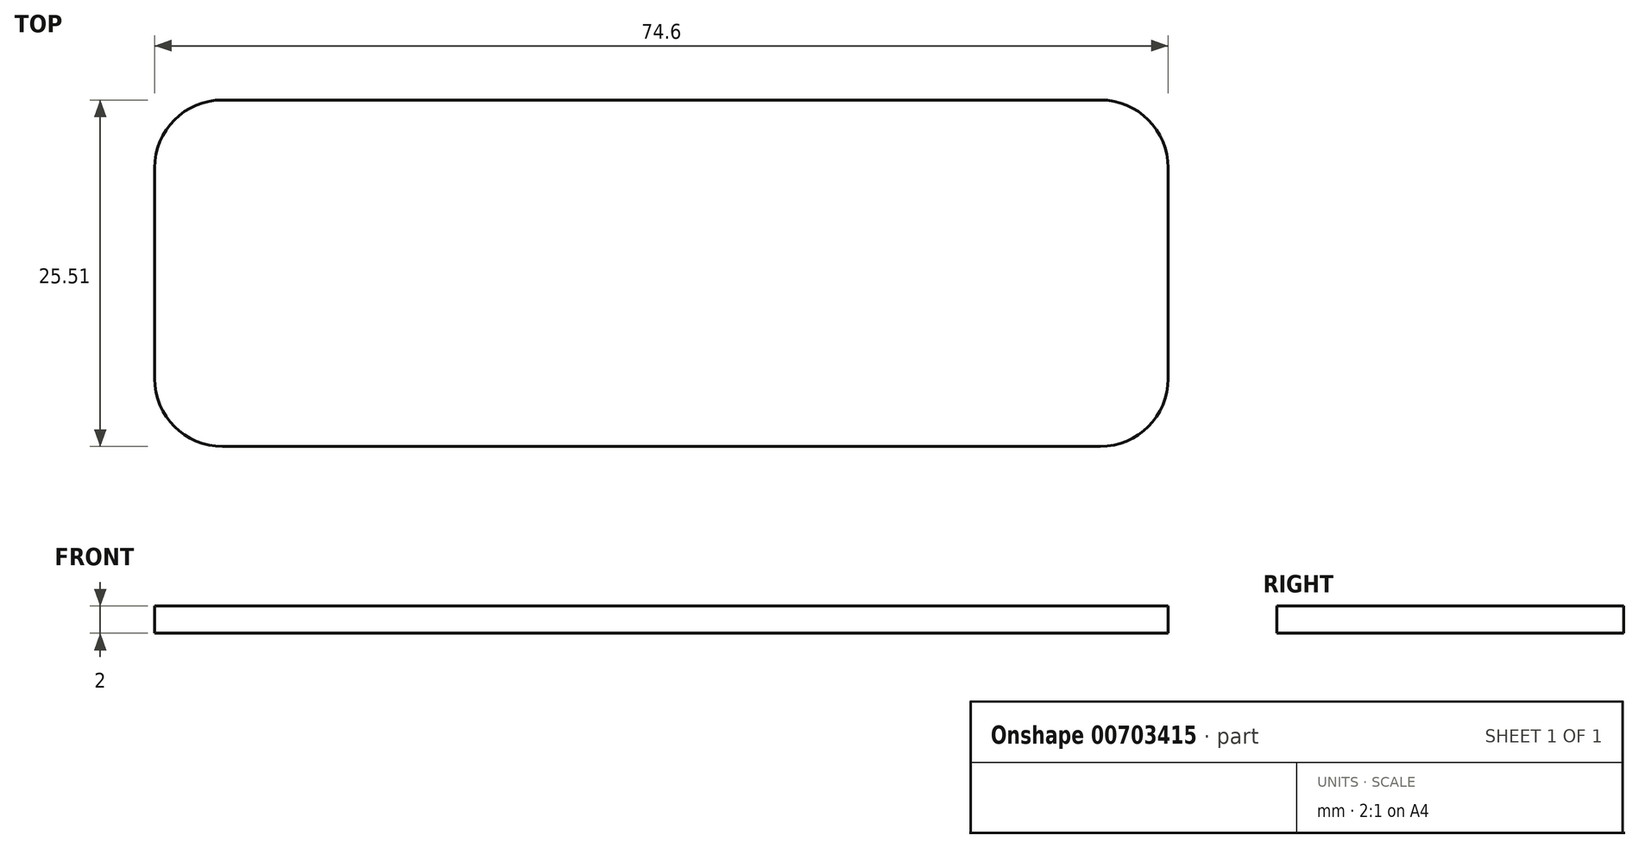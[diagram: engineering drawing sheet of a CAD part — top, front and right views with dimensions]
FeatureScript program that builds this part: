
annotation { "Feature Type Name" : "Feature", "Feature Type Description" : "" }
export const myFeature = defineFeature(function(context is Context, id is Id, definition is map)
    precondition{}
    {
        {
            var Q0;
            Q0=qCreatedBy(makeId("Top.planeOp"),FACE);
            var sketch = newSketch(context, id + "F0", { "sketchPlane" : qUnion([Q0])});
            skLineSegment(sketch, "E0.bottom", {"start": v(-31.4, 11.94) * mm, "end": v(33.19, 11.94) * mm});
            skLineSegment(sketch, "E0.top", {"start": v(-31.4, -13.57) * mm, "end": v(33.19, -13.57) * mm});
            skLineSegment(sketch, "E0.left", {"start": v(-36.4, 6.94) * mm, "end": v(-36.4, -8.57) * mm});
            skLineSegment(sketch, "E0.right", {"start": v(38.19, 6.94) * mm, "end": v(38.19, -8.57) * mm});
            skPoint(sketch, "E1.visualSharp", {"position": v(-36.4, 11.94) * mm});
            skArc(sketch, "E1.filletArc", {"start": v(-31.4, 11.94) * mm, "mid": v(-34.94, 10.48) * mm, "end": v(-36.4, 6.94) * mm});
            skPoint(sketch, "E2.visualSharp", {"position": v(-36.4, -13.57) * mm});
            skArc(sketch, "E2.filletArc", {"start": v(-36.4, -8.57) * mm, "mid": v(-34.94, -12.1) * mm, "end": v(-31.4, -13.57) * mm});
            skPoint(sketch, "E3.visualSharp", {"position": v(38.19, -13.57) * mm});
            skArc(sketch, "E3.filletArc", {"start": v(33.19, -13.57) * mm, "mid": v(36.72, -12.1) * mm, "end": v(38.19, -8.57) * mm});
            skPoint(sketch, "E4.visualSharp", {"position": v(38.19, 11.94) * mm});
            skArc(sketch, "E4.filletArc", {"start": v(38.19, 6.94) * mm, "mid": v(36.72, 10.48) * mm, "end": v(33.19, 11.94) * mm});
            skSolve(sketch);
        }
        {
            var Q0;
            Q0=makeQuery(id+"F0.imprint","IMPRINT",FACE,{"disambiguationData":[TD([[makeQuery(id+"F0.imprint","IMPRINT",EDGE,{"derivedFrom":sQuery(id+"F0.wireOp",EDGE,"E0.bottom")}),-1.0]])]});
            extrude(context, id + "F1", {"entities" : qUnion([Q0]), "depth" : 2 * mm, "offsetDistance" : 25.4 * mm});
        }
        {
            var Q0;
            Q0=makeQuery(id+"F1.opExtrude","CAP_FACE",FACE,{"disambiguationData":[OSD([sQuery(id+"F0.wireOp",EDGE,"E0.bottom"),sQuery(id+"F0.wireOp",EDGE,"E0.top"),sQuery(id+"F0.wireOp",EDGE,"E0.left"),sQuery(id+"F0.wireOp",EDGE,"E0.right"),sQuery(id+"F0.wireOp",EDGE,"E1.filletArc"),sQuery(id+"F0.wireOp",EDGE,"E2.filletArc"),sQuery(id+"F0.wireOp",EDGE,"E3.filletArc"),sQuery(id+"F0.wireOp",EDGE,"E4.filletArc")])],"isStart":false});
            var sketch = newSketch(context, id + "F2", { "sketchPlane" : qUnion([Q0])});
            skCircle(sketch, "E5", {"center": v(-31.4, 6.94) * mm, "radius": 2.83 * mm});
            skSolve(sketch);
        }
        {
            var Q0;
            Q0=sQuery(id+"F2.wireOp",EDGE,"E5");
            extrude(context, id + "F3", {"bodyType" : ToolBodyType.SURFACE, "surfaceEntities" : qUnion([Q0]), "depth" : 25.4 * mm, "offsetDistance" : 25.4 * mm});
        }
    });
